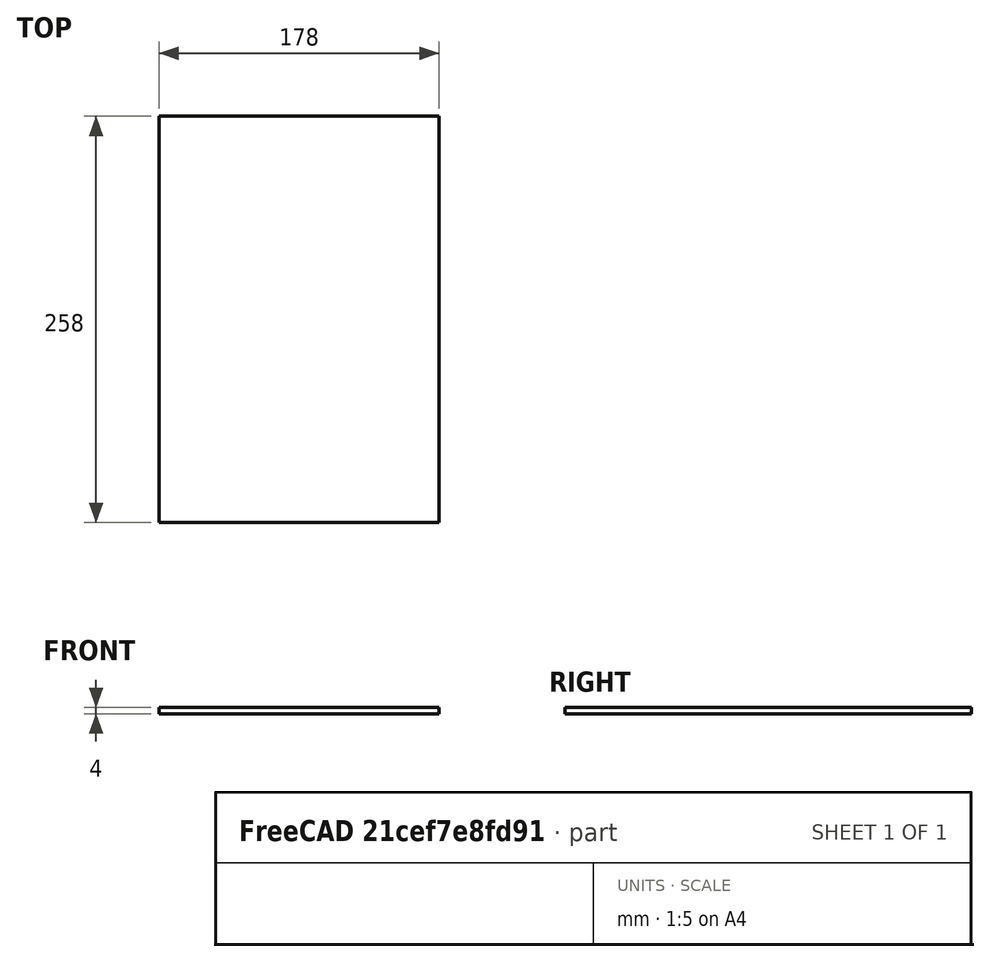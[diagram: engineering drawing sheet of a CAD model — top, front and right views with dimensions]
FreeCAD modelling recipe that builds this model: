
FCSTD DOCUMENT  (FreeCAD 0.17R13528 (Git))
Label: GlassDarkFront
License: All rights reserved
LicenseURL: http://en.wikipedia.org/wiki/All_rights_reserved
objects: Sketcher::SketchObject×1, PartDesign::Pad×1, PartDesign::Body×1
note: 4 computed .brp shape members not serialized (recipe doc carries the construction recipe); baked Part::Feature solids carry a one-line shape summary decoded from their .brp

FEATURE [Sketcher::SketchObject] Sketch
  MapMode = 5
  Support = -> [XY_Plane]
  expr: Constraints.width = 170 + 4 + 4
  sketch-geometry (4):
    g0: LineSegment StartX=0 StartY=0 StartZ=0 EndX=0 EndY=258 EndZ=0
    g1: LineSegment StartX=0 StartY=258 StartZ=0 EndX=178 EndY=258 EndZ=0
    g2: LineSegment StartX=178 StartY=258 StartZ=0 EndX=178 EndY=0 EndZ=0
    g3: LineSegment StartX=178 StartY=0 StartZ=0 EndX=0 EndY=0 EndZ=0
  constraints (12):
    c: Coincident(g0,g-1)
    c: Vertical(g0)
    c: Coincident(g1,g0)
    c: Horizontal(g1)
    c: Coincident(g2,g1)
    c: Vertical(g2)
    c: Coincident(g3,g2)
    c: PointOnObject(g3,g-1)
    c: Horizontal(g3)
    c: Coincident(g3,g-1)
    c: DistanceX(g3,g3) = 178  'width'
    c: DistanceY(g0,g0) = 258  'height'
FEATURE [PartDesign::Pad] Pad
  Length = 4
  Length2 = 100
  Profile = -> Sketch
  Type = 0
  expr: Length = Data#Spreadsheet.B1
FEATURE [PartDesign::Body] Body
  Group = -> [Sketch,Pad]
  Origin = -> Origin
  Tip = -> Pad
